# Revit family: Roof_Hatch-Best-Access-Doors-Domed-BA-GRH-DO_Series
name_source: partatom
category: Specialty Equipment
revit_build: Autodesk Revit 2017 (Build: 20160225_1515(x64)
units: mm (PartAtom-declared; Revit-internal decimal feet)

## family parameters
Cut with Voids When Loaded = Yes
Host = Face
OmniClass Number = 23.40.00.00
Part Type = Normal
Room Calculation Point = No
Round Connector Dimension = Use Diameter
Shared = Yes

## types (5) — shared parameters
Assembly Code = C1020700
Default Elevation = 0"
Description = Galvanized Steel Domed Roof Hatch
Finish = Galvanized Steel-Best Access Doors-14 Gauge-Polyester Grey Enamel
Installation Type = Surface Mount
Length = 12"
Manufacturer = Best Access Door
Material = Galvanized Steel-Best Access Doors-14 Gauge-Polyester Grey Enamel
Product data url = https://bimobject.com
Revised Date = 08/29/2018
URL = https://www.bestaccessdoors.com

## per-type parameters (varying)
| type | Height | Width |
| BA-GRH-DO-3232 | 24" | 24" |
| BA-GRH-DO-3244 | 36" | 24" |
| BA-GRH-DO-3838 | 30" | 30" |
| BA-GRH-DO-3844 | 36" | 30" |
| BA-GRH-DO-4444 | 36" | 36" |

note: column(s) folded — value = type name in every type: Model

## geometry (parser evidence)
native form markers: Sweep x1
no freeform markers — native parametric forms only
